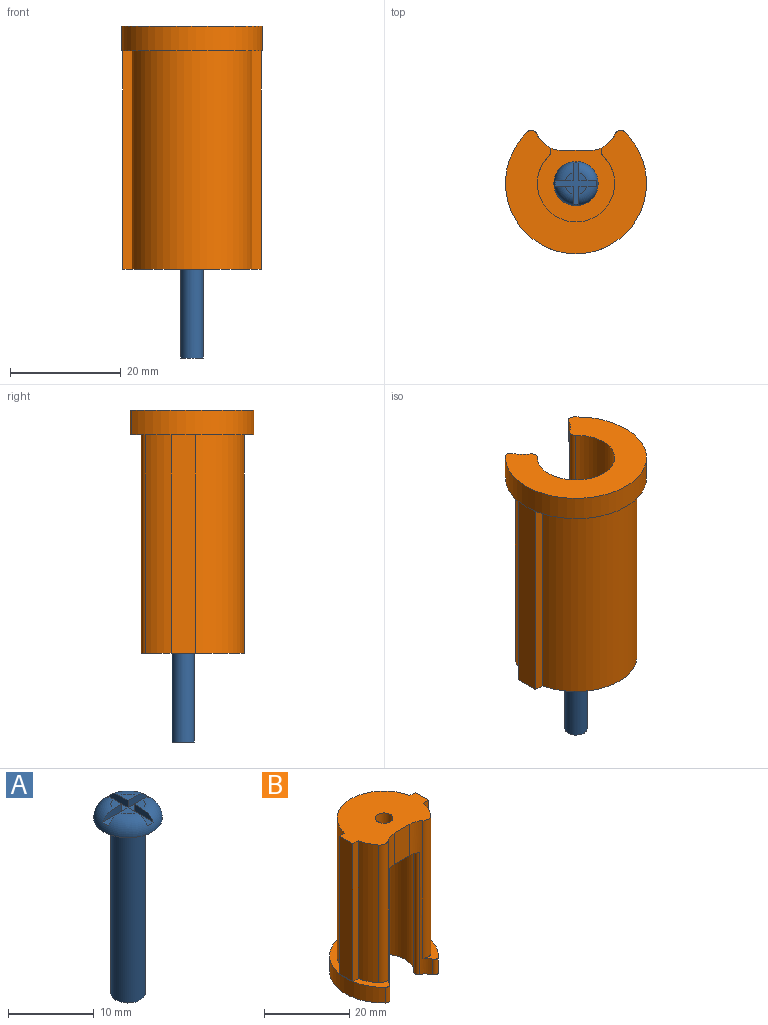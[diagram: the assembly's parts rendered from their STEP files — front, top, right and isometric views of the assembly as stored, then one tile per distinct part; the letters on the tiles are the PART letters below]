
ASSEMBLY  parts=2 mates=1
PART A: 17 faces, bbox 8.7x8.7x27 mm
  f0: plane 1.44x1.44mm, normal (0,0,1), area 1.4mm2, adj f3,f8,f9
  f1: plane 1.44x1.44mm, normal (0,0,1), area 1.4mm2, adj f3,f10,f11
  f2: plane 1.44x1.44mm, normal (0,0,1), area 1.4mm2, adj f3,f14,f15
  f3: torus R=2mm, axis (0,0,1), area 56.2mm2, adj f0,f1,f2,f4,f5,f8,f9,f10
  f4: plane 1.44x1.44mm, normal (0,0,1), area 1.4mm2, adj f3,f12,f13
  f5: plane 8x8mm, normal (0,0,-1), area 37.7mm2, adj f3,f6
  f6: cylinder r=2mm len=25mm, axis (0,0,1), area 314.2mm2, adj f5,f7
  f7: plane 4x4mm, normal (0,0,-1), area 12.6mm2, adj f6
  f8: plane 3.2x1mm, normal (0,-1,0), area 2.7mm2, adj f0,f3,f9,f16
  f9: plane 3.2x1mm, normal (-1,0,0), area 2.7mm2, adj f0,f3,f8,f16
  f10: plane 3.2x1mm, normal (1,0,0), area 2.7mm2, adj f1,f3,f11,f16
  f11: plane 3.2x1mm, normal (0,-1,0), area 2.7mm2, adj f1,f3,f10,f16
  f12: plane 3.2x1mm, normal (0,1,0), area 2.7mm2, adj f3,f4,f13,f16
  f13: plane 3.2x1mm, normal (1,0,0), area 2.7mm2, adj f3,f4,f12,f16
  f14: plane 3.2x1mm, normal (-1,0,0), area 2.7mm2, adj f2,f3,f15,f16
  f15: plane 3.2x1mm, normal (0,1,0), area 2.7mm2, adj f2,f3,f14,f16
  f16: plane 7.46x7.46mm, normal (0,0,1), area 13.9mm2, adj f3,f8,f9,f10,f11,f12,f13,f14
PART B: 25 faces, bbox 25.5x22.3x44 mm
  f0: plane 25.5x22.32mm, normal (0,0,1), area 90.3mm2, adj f1,f2,f7,f8,f10,f11,f12,f13
  f1: cylinder r=11mm len=39.5mm, axis (0,0,1), area 205.7mm2, adj f0,f4,f12,f19
  f2: cylinder r=12.75mm len=25.5mm, axis (0,0,-1), area 274.1mm2, adj f0,f3,f23,f24
  f3: plane 25.5x22.32mm, normal (0,0,-1), area 280.1mm2, adj f2,f5,f17,f18,f21,f22,f23,f24
  f4: plane 25x18.62mm, normal (0,0,1), area 326.2mm2, adj f1,f7,f8,f9,f10,f11,f12,f13
  f5: cylinder r=7mm len=35mm, axis (0,0,-1), area 1166.1mm2, adj f3,f6,f21,f22
  f6: plane 14x13.66mm, normal (0,0,-1), area 136.5mm2, adj f5,f9,f16,f17,f18,f21,f22
  f7: cylinder r=11mm len=39.5mm, axis (0,0,1), area 1190mm2, adj f0,f4,f10,f13
  f8: cylinder r=11mm len=39.5mm, axis (0,0,1), area 205.7mm2, adj f0,f4,f14,f20
  f9: cylinder r=2.1mm len=9mm, axis (0,0,1), area 118.8mm2, adj f4,f6
  f10: plane 39.5x1.72mm, normal (0,1,0), area 68mm2, adj f0,f4,f7,f11
  f11: plane 39.5x4.4mm, normal (-1,0,0), area 173.8mm2, adj f0,f4,f10,f12
  f12: plane 39.5x1.72mm, normal (0,-1,0), area 68mm2, adj f0,f1,f4,f11
  f13: plane 39.5x1.72mm, normal (0,1,0), area 68mm2, adj f0,f4,f7,f15
  f14: plane 39.5x1.72mm, normal (0,-1,0), area 68mm2, adj f0,f4,f8,f15
  f15: plane 39.5x4.4mm, normal (1,0,0), area 173.8mm2, adj f0,f4,f13,f14
  f16: plane 9x5.1mm, normal (0,-1,0), area 45.9mm2, adj f4,f6,f17,f18
  f17: cylinder r=5mm len=44mm, axis (0,0,-1), area 72.4mm2, adj f0,f3,f4,f6,f16,f20,f22,f24
  f18: cylinder r=5mm len=44mm, axis (0,0,-1), area 72.4mm2, adj f0,f3,f4,f6,f16,f19,f21,f23
  f19: cylinder r=2mm len=39.5mm, axis (0,0,-1), area 125.7mm2, adj f0,f1,f4,f18
  f20: cylinder r=2mm len=39.5mm, axis (0,0,1), area 125.7mm2, adj f0,f4,f8,f17
  f21: cylinder r=1mm len=35mm, axis (0,0,-1), area 65.1mm2, adj f3,f5,f6,f18
  f22: cylinder r=1mm len=35mm, axis (0,0,1), area 65.1mm2, adj f3,f5,f6,f17
  f23: cylinder r=1mm len=4.5mm, axis (0,0,1), area 8.6mm2, adj f0,f2,f3,f18
  f24: cylinder r=1mm len=4.5mm, axis (0,0,1), area 8.6mm2, adj f0,f2,f3,f17
PLACE A t=(-5.41,-8.1,-26.78)mm
PLACE B rot(axis=(1,0,0),180deg) t=(-5.41,-8.1,8.22)mm
MATE revolute B.f9 <-> A.f6  axis (0,0,1) through (-5.41,-8.1,-26.78)mm
